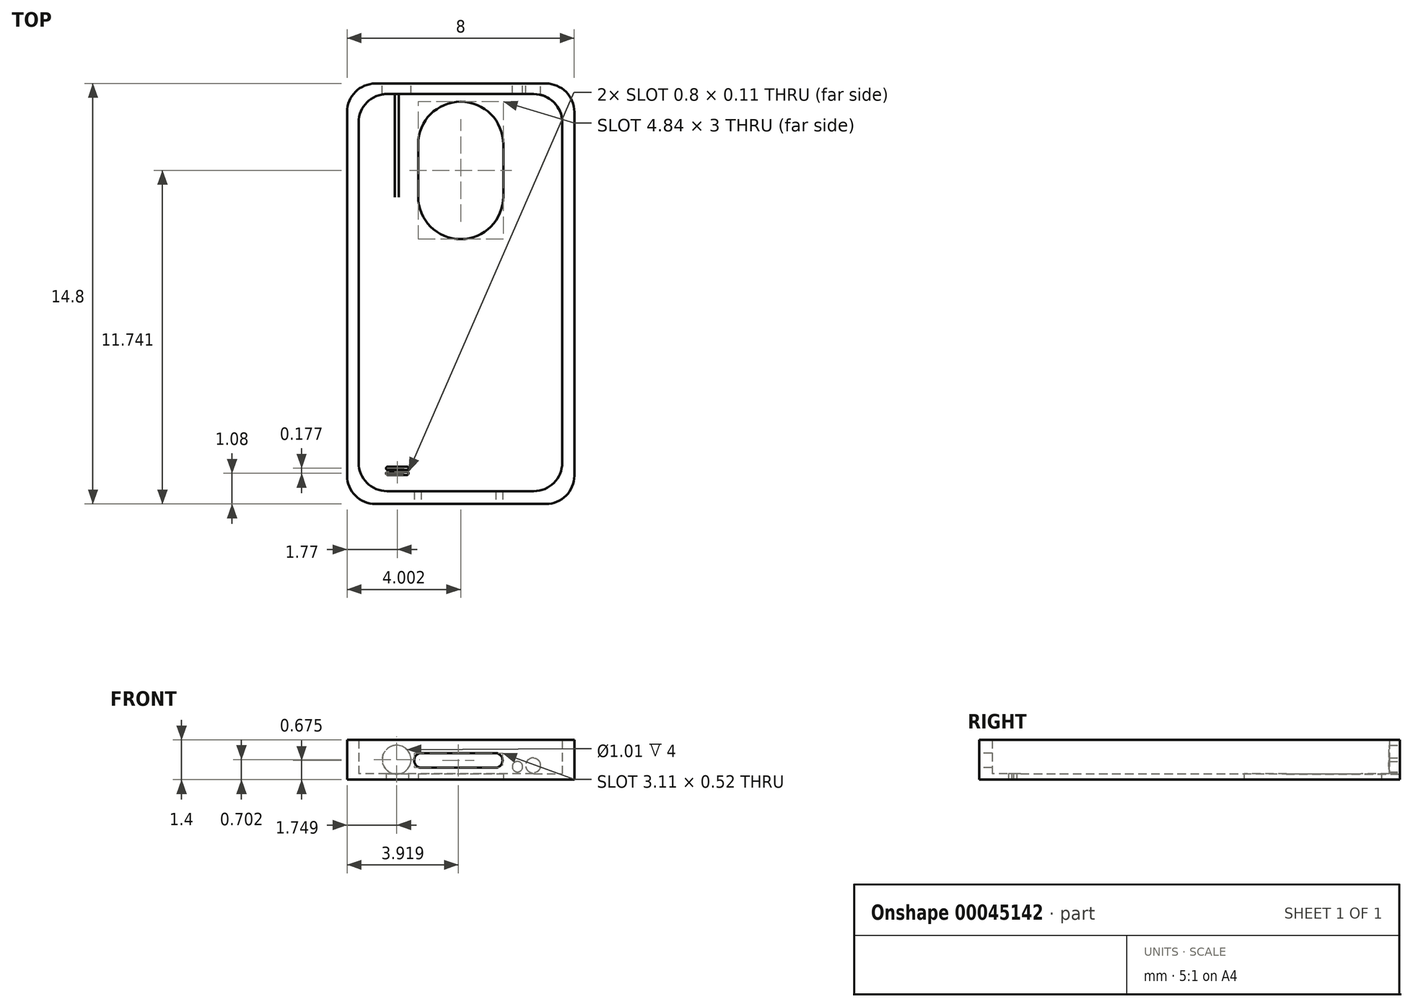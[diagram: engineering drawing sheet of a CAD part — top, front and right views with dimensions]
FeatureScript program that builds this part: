
annotation { "Feature Type Name" : "Feature", "Feature Type Description" : "" }
export const myFeature = defineFeature(function(context is Context, id is Id, definition is map)
    precondition{}
    {
        {
            var Q0;
            Q0=qCreatedBy(makeId("Top.planeOp"),FACE);
            var sketch = newSketch(context, id + "F0", { "sketchPlane" : qUnion([Q0])});
            skLineSegment(sketch, "E0.bottom", {"start": v(6.76, -2.45) * mm, "end": v(14.76, -2.45) * mm});
            skLineSegment(sketch, "E0.top", {"start": v(6.76, 12.35) * mm, "end": v(14.76, 12.35) * mm});
            skLineSegment(sketch, "E0.left", {"start": v(6.76, -2.45) * mm, "end": v(6.76, 12.35) * mm});
            skLineSegment(sketch, "E0.right", {"start": v(14.76, -2.45) * mm, "end": v(14.76, 12.35) * mm});
            skLineSegment(sketch, "E1.bottom", {"start": v(14.34, -2) * mm, "end": v(7.17, -2) * mm});
            skLineSegment(sketch, "E1.top", {"start": v(14.34, 11.98) * mm, "end": v(7.17, 11.98) * mm});
            skLineSegment(sketch, "E1.left", {"start": v(14.34, -2) * mm, "end": v(14.34, 11.98) * mm});
            skLineSegment(sketch, "E1.right", {"start": v(7.17, -2) * mm, "end": v(7.17, 11.98) * mm});
            skSolve(sketch);
        }
        {
            var Q0;
            Q0=makeQuery(id+"F0.imprint","IMPRINT",FACE,{"disambiguationData":[TD([[makeQuery(id+"F0.imprint","IMPRINT",EDGE,{"derivedFrom":sQuery(id+"F0.wireOp",EDGE,"E0.bottom")}),1.0]])]});
            extrude(context, id + "F1", {"entities" : qUnion([Q0]), "depth" : 1.4 * mm});
        }
        {
            var Q0;
            Q0=makeQuery(id+"F1.opExtrude","SWEPT_EDGE",EDGE,{"disambiguationData":[OSD([sQuery(id+"F0.wireOp",EDGE,"E0.top"),sQuery(id+"F0.wireOp",EDGE,"E0.left")])]});
            var Q1;
            Q1=makeQuery(id+"F1.opExtrude","SWEPT_EDGE",EDGE,{"disambiguationData":[OSD([sQuery(id+"F0.wireOp",EDGE,"E0.bottom"),sQuery(id+"F0.wireOp",EDGE,"E0.left")])]});
            var Q2;
            Q2=makeQuery(id+"F1.opExtrude","SWEPT_EDGE",EDGE,{"disambiguationData":[OSD([sQuery(id+"F0.wireOp",EDGE,"E0.bottom"),sQuery(id+"F0.wireOp",EDGE,"E0.right")])]});
            var Q3;
            Q3=makeQuery(id+"F1.opExtrude","SWEPT_EDGE",EDGE,{"disambiguationData":[OSD([sQuery(id+"F0.wireOp",EDGE,"E0.top"),sQuery(id+"F0.wireOp",EDGE,"E0.right")])]});
            var Q4;
            Q4=makeQuery(id+"F1.opExtrude","SWEPT_EDGE",EDGE,{"disambiguationData":[OSD([sQuery(id+"F0.wireOp",EDGE,"E1.top"),sQuery(id+"F0.wireOp",EDGE,"E1.right")])]});
            var Q5;
            Q5=makeQuery(id+"F1.opExtrude","SWEPT_EDGE",EDGE,{"disambiguationData":[OSD([sQuery(id+"F0.wireOp",EDGE,"E1.top"),sQuery(id+"F0.wireOp",EDGE,"E1.left")])]});
            var Q6;
            Q6=makeQuery(id+"F1.opExtrude","SWEPT_EDGE",EDGE,{"disambiguationData":[OSD([sQuery(id+"F0.wireOp",EDGE,"E1.bottom"),sQuery(id+"F0.wireOp",EDGE,"E1.left")])]});
            var Q7;
            Q7=makeQuery(id+"F1.opExtrude","SWEPT_EDGE",EDGE,{"disambiguationData":[OSD([sQuery(id+"F0.wireOp",EDGE,"E1.bottom"),sQuery(id+"F0.wireOp",EDGE,"E1.right")])]});
            fillet(context, id + "F2", {"entities" : qUnion([Q0, Q1, Q2, Q3, Q4, Q5, Q6, Q7]), "radius" : 1 * mm, "tangentPropagation" : true, "allowEdgeOverflow" : false});
        }
        {
            var Q0;
            Q0=makeQuery(id+"F0.imprint","IMPRINT",FACE,{"disambiguationData":[TD([[makeQuery(id+"F0.imprint","IMPRINT",EDGE,{"derivedFrom":sQuery(id+"F0.wireOp",EDGE,"E1.bottom")}),-1.0]])]});
            extrude(context, id + "F3", {"entities" : qUnion([Q0]), "operationType" : NewBodyOperationType.ADD, "depth" : .2 * mm});
        }
        {
            var Q0;
            Q0=makeQuery(id+"F1.opExtrude","SWEPT_FACE",FACE,{"disambiguationData":[OSD([sQuery(id+"F0.wireOp",EDGE,"E1.right")])]});
            extrude(context, id + "F4", {"entities" : qUnion([Q0]), "operationType" : NewBodyOperationType.ADD, "oppositeDirection" : true, "depth" : 0.2 * mm});
        }
        {
            var Q0;
            Q0=makeQuery(id+"F1.opExtrude","SWEPT_FACE",FACE,{"disambiguationData":[OSD([sQuery(id+"F0.wireOp",EDGE,"E0.bottom")])]});
            var sketch = newSketch(context, id + "F5", { "sketchPlane" : qUnion([Q0])});
            skLineSegment(sketch, "E2.bottom", {"start": v(8.93, 1.19) * mm, "end": v(12.43, 1.19) * mm});
            skLineSegment(sketch, "E2.top", {"start": v(8.93, 0.19) * mm, "end": v(12.43, 0.19) * mm});
            skLineSegment(sketch, "E2.left", {"start": v(8.93, 1.19) * mm, "end": v(8.93, 0.19) * mm});
            skLineSegment(sketch, "E2.right", {"start": v(12.43, 1.19) * mm, "end": v(12.43, 0.19) * mm});
            skLineSegment(sketch, "E3", {"start": v(9.38, 0.93) * mm, "end": v(11.98, 0.93) * mm});
            skLineSegment(sketch, "E4", {"start": v(9.37, 0.42) * mm, "end": v(12, 0.42) * mm});
            skArc(sketch, "E5", {"start": v(9.38, 0.93) * mm, "mid": v(9.12, 0.68) * mm, "end": v(9.37, 0.42) * mm});
            skArc(sketch, "E6", {"start": v(11.98, 0.93) * mm, "mid": v(12.24, 0.69) * mm, "end": v(12, 0.42) * mm});
            skSolve(sketch);
        }
        {
            var Q0;
            Q0=makeQuery(id+"F5.imprint","IMPRINT",FACE,{"disambiguationData":[TD([[makeQuery(id+"F5.imprint","IMPRINT",EDGE,{"derivedFrom":sQuery(id+"F5.wireOp",EDGE,"E3")}),-1.0]])]});
            extrude(context, id + "F6", {"entities" : qUnion([Q0]), "operationType" : NewBodyOperationType.REMOVE, "oppositeDirection" : true, "depth" : 4 * mm});
        }
        {
            var Q0;
            Q0=makeQuery(id+"F1.opExtrude","SWEPT_FACE",FACE,{"disambiguationData":[OSD([sQuery(id+"F0.wireOp",EDGE,"E0.top")])]});
            var sketch = newSketch(context, id + "F7", { "sketchPlane" : qUnion([Q0])});
            skCircle(sketch, "E7", {"center": v(-8.5, 0.7) * mm, "radius": 0.5 * mm});
            skCircle(sketch, "E8", {"center": v(-13.31, 0.5) * mm, "radius": 0.26 * mm});
            skCircle(sketch, "E9", {"center": v(-12.76, 0.45) * mm, "radius": 0.18 * mm});
            skSolve(sketch);
        }
        {
            var Q0;
            Q0=makeQuery(id+"F7.imprint","IMPRINT",FACE,{"disambiguationData":[TD([[makeQuery(id+"F7.imprint","IMPRINT",EDGE,{"derivedFrom":sQuery(id+"F7.wireOp",EDGE,"E7")}),1.0]])]});
            var Q1;
            Q1=makeQuery(id+"F7.imprint","IMPRINT",FACE,{"disambiguationData":[TD([[makeQuery(id+"F7.imprint","IMPRINT",EDGE,{"derivedFrom":sQuery(id+"F7.wireOp",EDGE,"E9")}),1.0]])]});
            var Q2;
            Q2=makeQuery(id+"F7.imprint","IMPRINT",FACE,{"disambiguationData":[TD([[makeQuery(id+"F7.imprint","IMPRINT",EDGE,{"derivedFrom":sQuery(id+"F7.wireOp",EDGE,"E8")}),1.0]])]});
            extrude(context, id + "F8", {"entities" : qUnion([Q0, Q1, Q2]), "operationType" : NewBodyOperationType.REMOVE, "oppositeDirection" : true, "depth" : 4 * mm});
        }
        {
            var Q0;
            {var subQ0=sQuery(id+"F0.wireOp",EDGE,"E1.bottom");var subQ1=sQuery(id+"F0.wireOp",EDGE,"E1.top");var subQ2=sQuery(id+"F0.wireOp",EDGE,"E1.left");var subQ3=sQuery(id+"F0.wireOp",EDGE,"E1.right");Q0=makeQuery(id+"F3.boolean.opBoolean","MERGE",FACE,{"derivedFrom":[makeQuery(id+"F1.opExtrude","CAP_FACE",FACE,{"disambiguationData":[OSD([sQuery(id+"F0.wireOp",EDGE,"E0.bottom"),sQuery(id+"F0.wireOp",EDGE,"E0.top"),sQuery(id+"F0.wireOp",EDGE,"E0.left"),sQuery(id+"F0.wireOp",EDGE,"E0.right"),subQ0,subQ1,subQ2,subQ3])],"isStart":true}),makeQuery(id+"F3.opExtrude","CAP_FACE",FACE,{"disambiguationData":[OSD([subQ0,subQ1,subQ2,subQ3])],"isStart":true})]});}
            var sketch = newSketch(context, id + "F9", { "sketchPlane" : qUnion([Q0])});
            skLineSegment(sketch, "E10", {"start": v(8.87, 1.25) * mm, "end": v(8.19, 1.25) * mm});
            skLineSegment(sketch, "E11", {"start": v(8.87, 1.14) * mm, "end": v(8.19, 1.14) * mm});
            skArc(sketch, "E12", {"start": v(8.87, 1.14) * mm, "mid": v(8.93, 1.2) * mm, "end": v(8.87, 1.25) * mm});
            skArc(sketch, "E13", {"start": v(8.19, 1.14) * mm, "mid": v(8.13, 1.2) * mm, "end": v(8.19, 1.25) * mm});
            skLineSegment(sketch, "E14.MirrorCS", {"start": v(8.87, 1.31) * mm, "end": v(8.19, 1.31) * mm});
            skLineSegment(sketch, "E15.MirrorCS", {"start": v(8.87, 1.43) * mm, "end": v(8.19, 1.43) * mm});
            skArc(sketch, "E16.MirrorCS", {"start": v(8.87, 1.43) * mm, "mid": v(8.93, 1.37) * mm, "end": v(8.87, 1.31) * mm});
            skArc(sketch, "E17.MirrorCS", {"start": v(8.19, 1.43) * mm, "mid": v(8.13, 1.37) * mm, "end": v(8.19, 1.31) * mm});
            skSolve(sketch);
        }
        {
            var Q0;
            Q0=makeQuery(id+"F9.imprint","IMPRINT",FACE,{"disambiguationData":[TD([[makeQuery(id+"F9.imprint","IMPRINT",EDGE,{"derivedFrom":sQuery(id+"F9.wireOp",EDGE,"E14.MirrorCS")}),-1.0]])]});
            var Q1;
            Q1=makeQuery(id+"F9.imprint","IMPRINT",FACE,{"disambiguationData":[TD([[makeQuery(id+"F9.imprint","IMPRINT",EDGE,{"derivedFrom":sQuery(id+"F9.wireOp",EDGE,"E10")}),1.0]])]});
            extrude(context, id + "F10", {"entities" : qUnion([Q0, Q1]), "operationType" : NewBodyOperationType.REMOVE, "oppositeDirection" : true, "depth" : 4 * mm});
        }
        {
            var Q0;
            {var subQ0=sQuery(id+"F0.wireOp",EDGE,"E1.bottom");var subQ1=sQuery(id+"F0.wireOp",EDGE,"E1.top");var subQ2=sQuery(id+"F0.wireOp",EDGE,"E1.left");var subQ3=sQuery(id+"F0.wireOp",EDGE,"E1.right");Q0=makeQuery(id+"F3.boolean.opBoolean","MERGE",FACE,{"derivedFrom":[makeQuery(id+"F1.opExtrude","CAP_FACE",FACE,{"disambiguationData":[OSD([sQuery(id+"F0.wireOp",EDGE,"E0.bottom"),sQuery(id+"F0.wireOp",EDGE,"E0.top"),sQuery(id+"F0.wireOp",EDGE,"E0.left"),sQuery(id+"F0.wireOp",EDGE,"E0.right"),subQ0,subQ1,subQ2,subQ3])],"isStart":true}),makeQuery(id+"F3.opExtrude","CAP_FACE",FACE,{"disambiguationData":[OSD([subQ0,subQ1,subQ2,subQ3])],"isStart":true})]});}
            var sketch = newSketch(context, id + "F11", { "sketchPlane" : qUnion([Q0])});
            skLineSegment(sketch, "E18", {"start": v(12.26, -10.21) * mm, "end": v(12.26, -8.37) * mm});
            skLineSegment(sketch, "E19", {"start": v(9.26, -8.37) * mm, "end": v(9.26, -10.21) * mm});
            skArc(sketch, "E20", {"start": v(12.26, -8.37) * mm, "mid": v(10.76, -6.87) * mm, "end": v(9.26, -8.37) * mm});
            skArc(sketch, "E21", {"start": v(12.26, -10.21) * mm, "mid": v(10.76, -11.71) * mm, "end": v(9.26, -10.21) * mm});
            skSolve(sketch);
        }
        {
            var Q0;
            Q0=makeQuery(id+"F11.imprint","IMPRINT",FACE,{"disambiguationData":[TD([[makeQuery(id+"F11.imprint","IMPRINT",EDGE,{"derivedFrom":sQuery(id+"F11.wireOp",EDGE,"E18")}),1.0]])]});
            extrude(context, id + "F12", {"entities" : qUnion([Q0]), "operationType" : NewBodyOperationType.REMOVE, "oppositeDirection" : true, "depth" : 5 * mm});
        }
    });
